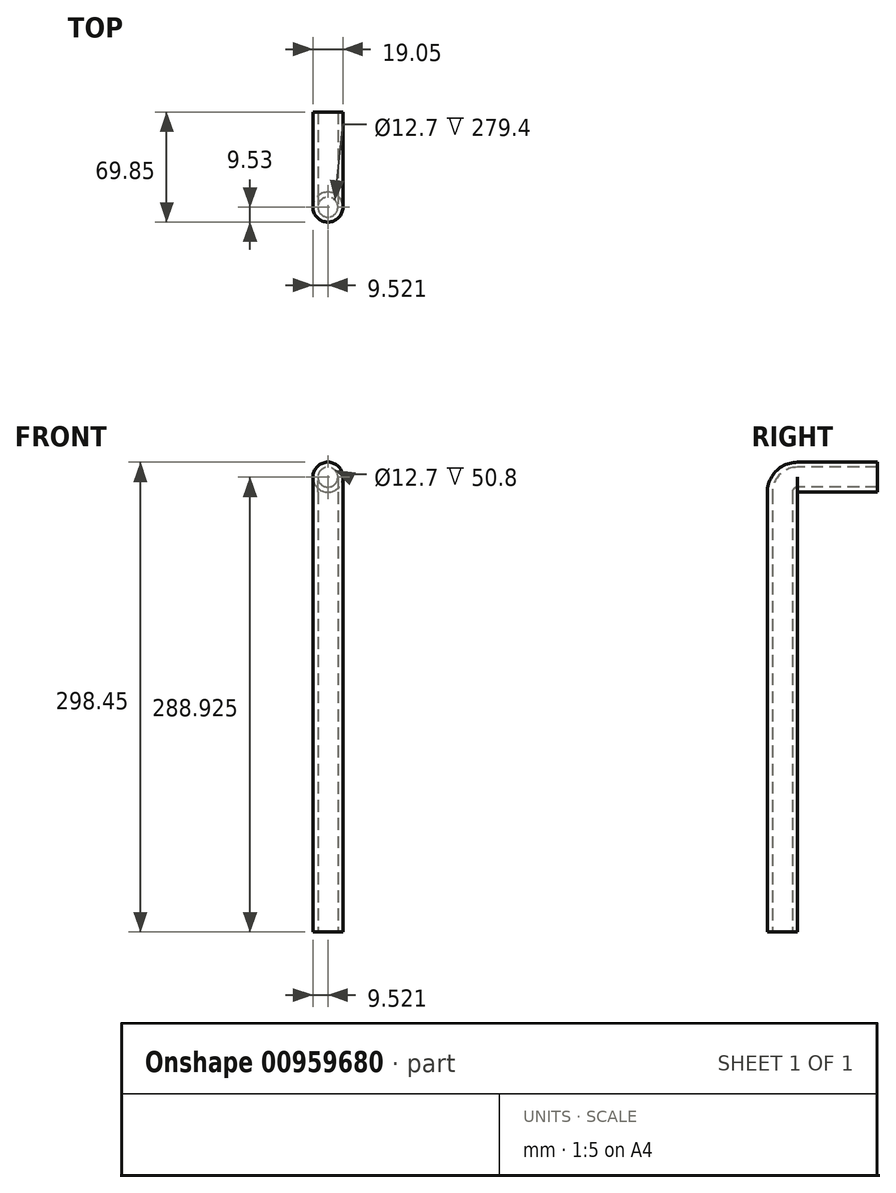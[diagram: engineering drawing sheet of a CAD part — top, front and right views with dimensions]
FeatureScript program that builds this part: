
annotation { "Feature Type Name" : "Feature", "Feature Type Description" : "" }
export const myFeature = defineFeature(function(context is Context, id is Id, definition is map)
    precondition{}
    {
        {
            var Q0;
            Q0=qCreatedBy(makeId("Top.planeOp"),FACE);
            var sketch = newSketch(context, id + "F0", { "sketchPlane" : qUnion([Q0])});
            skCircle(sketch, "E0", {"center": v(-22.17, 2.55) * mm, "radius": 9.53 * mm});
            skCircle(sketch, "E1", {"center": v(-22.17, 2.55) * mm, "radius": 6.35 * mm});
            skSolve(sketch);
        }
        {
            var Q0;
            Q0=makeQuery(id+"F0.imprint","IMPRINT",FACE,{"disambiguationData":[TD([[makeQuery(id+"F0.imprint","IMPRINT",EDGE,{"derivedFrom":sQuery(id+"F0.wireOp",EDGE,"E0")}),1.0]])]});
            extrude(context, id + "F1", {"entities" : qUnion([Q0]), "depth" : 279.4 * mm, "offsetDistance" : 25.4 * mm});
        }
        {
            var Q0;
            Q0=makeQuery(id+"F1.opExtrude","CAP_FACE",FACE,{"disambiguationData":[OSD([sQuery(id+"F0.wireOp",EDGE,"E0"),sQuery(id+"F0.wireOp",EDGE,"E1")])],"isStart":false});
            var sketch = newSketch(context, id + "F2", { "sketchPlane" : qUnion([Q0])});
            skLineSegment(sketch, "E2", {"start": v(-22.17, 12.07) * mm, "end": v(8.17, 12.07) * mm});
            skSolve(sketch);
        }
        {
            var Q0;
            Q0=makeQuery(id+"F2.imprint","IMPRINT",FACE,{"disambiguationData":[TD([[makeQuery(id+"F2.imprint","IMPRINT",EDGE,{"derivedFrom":makeQuery(id+"F1.opExtrude","CAP_EDGE",EDGE,{"disambiguationData":[OSD([sQuery(id+"F0.wireOp",EDGE,"E0")])],"isStart":false})}),1.0]])]});
            var Q1;
            Q1=sQuery(id+"F2.wireOp",EDGE,"E2");
            revolve(context, id + "F3", {"operationType" : NewBodyOperationType.ADD, "surfaceOperationType" : NewSurfaceOperationType.NEW, "entities" : qUnion([Q0]), "axis" : qUnion([Q1]), "revolveType" : RevolveType.ONE_DIRECTION, "oppositeDirection" : true, "angle" : 90 * degree});
        }
        {
            var Q0;
            Q0=makeQuery(id+"F3.opRevolve","CAP_FACE",FACE,{"disambiguationData":[OSD([sQuery(id+"F0.wireOp",EDGE,"E0"),sQuery(id+"F0.wireOp",EDGE,"E1")])],"isStart":false});
            extrude(context, id + "F4", {"entities" : qUnion([Q0]), "operationType" : NewBodyOperationType.ADD, "depth" : 50.8 * mm, "offsetDistance" : 25.4 * mm});
        }
    });
